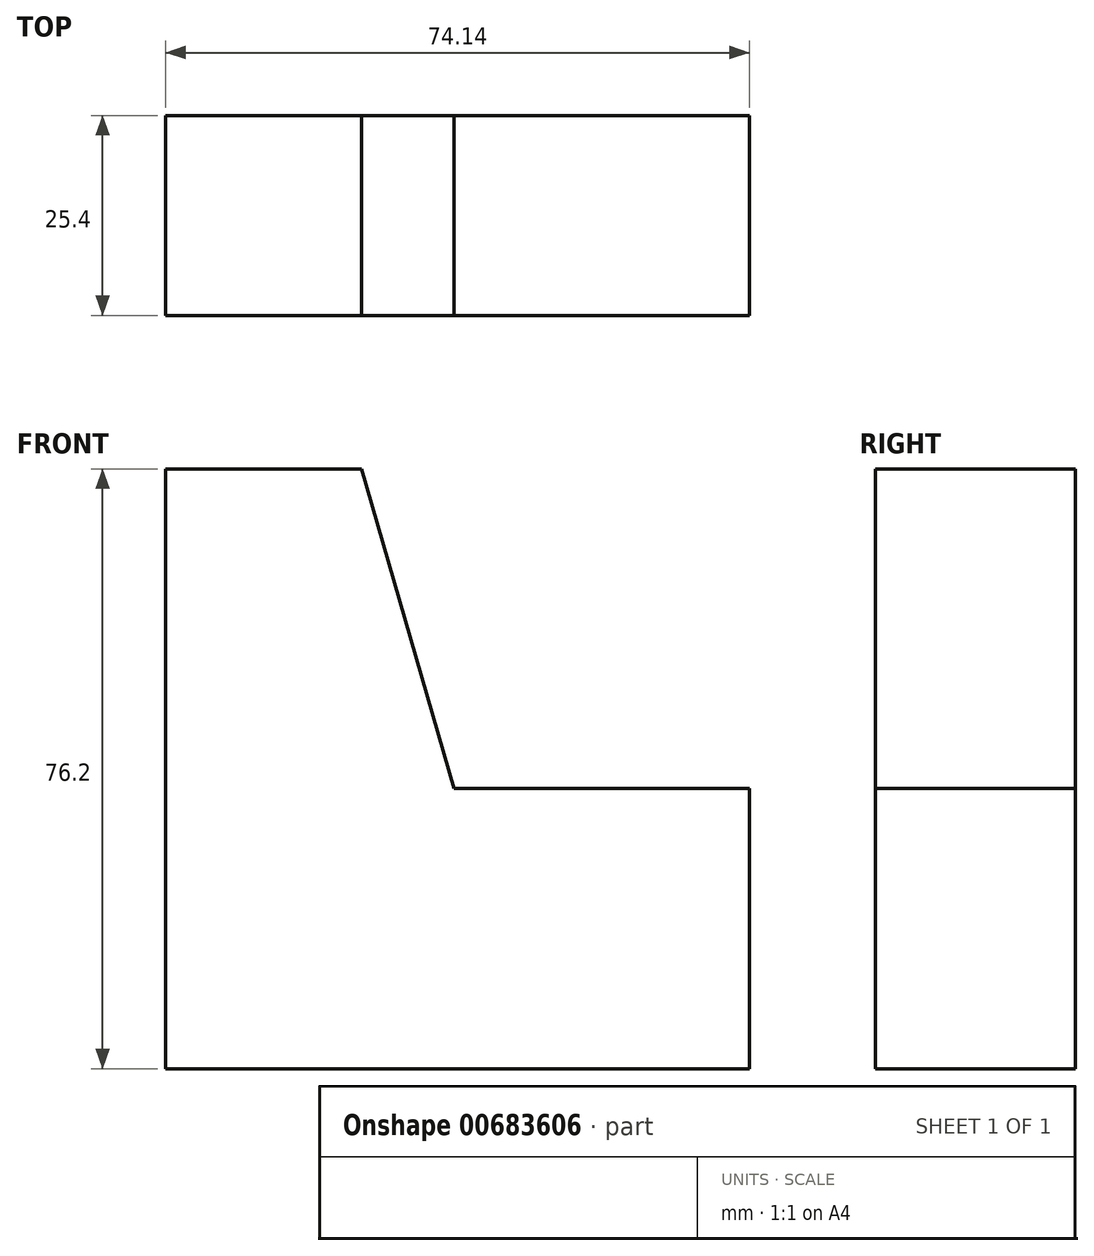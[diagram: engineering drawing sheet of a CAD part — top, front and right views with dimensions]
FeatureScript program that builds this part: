
annotation { "Feature Type Name" : "Feature", "Feature Type Description" : "" }
export const myFeature = defineFeature(function(context is Context, id is Id, definition is map)
    precondition{}
    {
        {
            var Q0;
            Q0=qCreatedBy(makeId("Front.planeOp"),FACE);
            var sketch = newSketch(context, id + "F0", { "sketchPlane" : qUnion([Q0])});
            skLineSegment(sketch, "E0.bottom", {"start": v(-19.5, 0) * mm, "end": v(-93.63, 0) * mm});
            skLineSegment(sketch, "E0.top", {"start": v(-68.73, 76.2) * mm, "end": v(-93.63, 76.2) * mm});
            skLineSegment(sketch, "E0.left", {"start": v(-19.5, 0) * mm, "end": v(-19.5, 35.58) * mm});
            skLineSegment(sketch, "E0.right", {"start": v(-93.63, 0) * mm, "end": v(-93.63, 76.2) * mm});
            skLineSegment(sketch, "E1", {"start": v(-68.73, 76.2) * mm, "end": v(-57, 35.58) * mm});
            skLineSegment(sketch, "E2", {"start": v(-57, 35.58) * mm, "end": v(-19.5, 35.58) * mm});
            skSolve(sketch);
        }
        {
            var Q0;
            Q0=makeQuery(id+"F0.imprint","IMPRINT",FACE,{"disambiguationData":[TD([[makeQuery(id+"F0.imprint","IMPRINT",EDGE,{"derivedFrom":sQuery(id+"F0.wireOp",EDGE,"E0.bottom")}),-1.0]])]});
            extrude(context, id + "F1", {"entities" : qUnion([Q0]), "depth" : 25.4 * mm, "offsetDistance" : 25.4 * mm});
        }
    });
